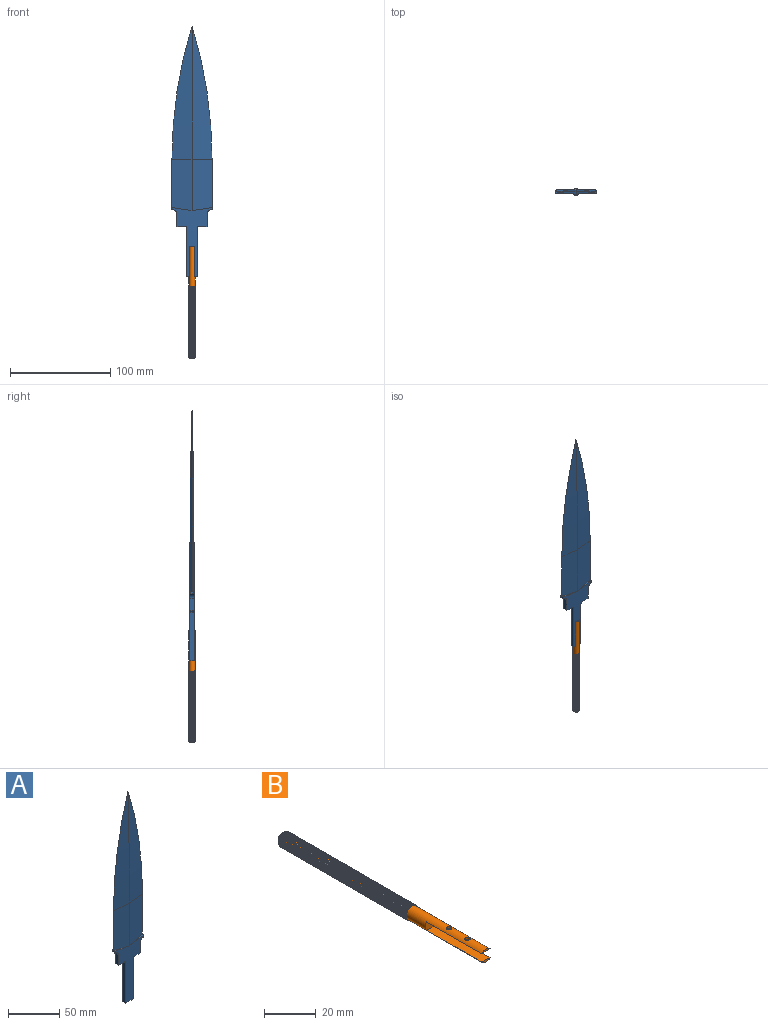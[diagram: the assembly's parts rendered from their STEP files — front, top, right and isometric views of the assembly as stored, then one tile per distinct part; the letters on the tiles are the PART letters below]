
ASSEMBLY  parts=2 mates=1
PART A: 31 faces, bbox 40.1x4.1x250.1 mm
  f0: plane 51x20mm, normal (0.1,-1,0), area 994.9mm2, adj f1,f2,f3,f21
  f1: plane 51x20mm, normal (-0.1,-1,0), area 994.9mm2, adj f0,f4,f5,f8
  f2: plane 51x20mm, normal (0.1,1,0), area 994.9mm2, adj f0,f5,f6,f10
  f3: cone r=432.23mm half-angle=84.3deg, axis (0,1,0), area 1790.2mm2, adj f0,f4,f6
  f4: cone r=452.22mm half-angle=84.3deg, axis (0,1,0), area 1790.2mm2, adj f1,f3,f7
  f5: plane 51x20mm, normal (-0.1,1,0), area 994.9mm2, adj f1,f2,f7,f9
  f6: cone r=452.22mm half-angle=84.3deg, axis (0,-1,0), area 1790.2mm2, adj f2,f3,f7
  f7: cone r=432.23mm half-angle=84.3deg, axis (0,-1,0), area 1790.2mm2, adj f4,f5,f6
  f8: plane 20.06x3.06mm, normal (0.15,0,0.99), area 20mm2, adj f1,f22,f25,f30
  f9: plane 20.06x3.06mm, normal (0.15,0,0.99), area 20mm2, adj f5,f22,f26,f28
  f10: plane 20.06x3.06mm, normal (-0.15,0,0.99), area 20mm2, adj f2,f20,f26,f27
  f11: plane 7.88x4mm, normal (0,0,-1), area 31.5mm2, adj f12,f24,f25,f26
  f12: cylinder r=2.12mm len=4mm, axis (0,1,0), area 13.3mm2, adj f11,f13,f25,f26
  f13: plane 47.88x4mm, normal (-1,0,0), area 191.5mm2, adj f12,f14,f25,f26
  f14: plane 10x4mm, normal (0,0,-1), area 40mm2, adj f13,f15,f25,f26
  f15: plane 47.88x4mm, normal (1,0,0), area 191.5mm2, adj f14,f16,f25,f26
  f16: cylinder r=2.12mm len=4mm, axis (0,1,0), area 13.3mm2, adj f15,f17,f25,f26
  f17: plane 7.88x4mm, normal (0,0,-1), area 31.5mm2, adj f16,f18,f25,f26
  f18: plane 12x4mm, normal (1,0,0), area 48mm2, adj f17,f19,f25,f26
  f19: cylinder r=5mm len=5mm, axis (0,1,0), area 31mm2, adj f18,f20,f25,f26,f27,f29
  f20: plane 2x2mm, normal (1,0,0), area 4mm2, adj f10,f19,f21,f27,f29
  f21: plane 20.06x3.06mm, normal (-0.15,0,0.99), area 20mm2, adj f0,f20,f25,f29
  f22: plane 2x2mm, normal (-1,0,0), area 4mm2, adj f8,f9,f23,f28,f30
  f23: cylinder r=5mm len=5mm, axis (0,1,0), area 31mm2, adj f22,f24,f25,f26,f28,f30
  f24: plane 12x4mm, normal (-1,0,0), area 48mm2, adj f11,f23,f25,f26
  f25: plane 68.85x38mm, normal (0,-1,0), area 1038.7mm2, adj f8,f11,f12,f13,f14,f15,f16,f17
  f26: plane 68.85x38mm, normal (0,1,0), area 1038.7mm2, adj f9,f10,f11,f12,f13,f14,f15,f16
  f27: cylinder r=1mm len=2.1mm, axis (0,0,1), area 3.1mm2, adj f10,f19,f20,f26
  f28: cylinder r=1mm len=2.1mm, axis (0,0,-1), area 3.1mm2, adj f9,f22,f23,f26
  f29: cylinder r=1mm len=2.1mm, axis (0,0,-1), area 3.1mm2, adj f19,f20,f21,f25
  f30: cylinder r=1mm len=2.1mm, axis (0,0,1), area 3.1mm2, adj f8,f22,f23,f25
PART B: 84 faces, bbox 6.6x111x7.6 mm
  f0: cylinder r=3mm len=6mm, axis (0,1,0), area 12.6mm2, adj f69,f77,f79,f81,f83
  f1: cylinder r=3mm len=41.68mm, axis (0,1,0), area 500.5mm2, adj f2,f70,f71,f72,f73,f74,f75,f76
  f2: cylinder r=3mm len=6mm, axis (0,1,0), area 11.3mm2, adj f1,f3,f79,f81
  f3: cylinder r=3mm len=6mm, axis (0,1,0), area 11.3mm2, adj f2,f4,f79,f81
  f4: cylinder r=3mm len=6mm, axis (0,1,0), area 11.3mm2, adj f3,f5,f79,f81
  f5: cylinder r=3mm len=6mm, axis (0,1,0), area 11.3mm2, adj f4,f6,f79,f81
  f6: cylinder r=3mm len=6mm, axis (0,1,0), area 11.3mm2, adj f5,f7,f79,f81
  f7: cylinder r=3mm len=6mm, axis (0,1,0), area 11.3mm2, adj f6,f8,f79,f81
  f8: cylinder r=3mm len=6mm, axis (0,1,0), area 11.3mm2, adj f7,f9,f79,f81
  f9: cylinder r=3mm len=6mm, axis (0,1,0), area 11.3mm2, adj f8,f10,f79,f81
  f10: cylinder r=3mm len=6mm, axis (0,1,0), area 11.3mm2, adj f9,f11,f79,f81
  f11: cylinder r=3mm len=6mm, axis (0,1,0), area 11.3mm2, adj f10,f12,f79,f81
  f12: cylinder r=3mm len=6mm, axis (0,1,0), area 11.3mm2, adj f11,f13,f79,f81
  f13: cylinder r=3mm len=6mm, axis (0,1,0), area 11.3mm2, adj f12,f14,f79,f81
  f14: cylinder r=3mm len=6mm, axis (0,1,0), area 11.3mm2, adj f13,f15,f79,f81
  f15: cylinder r=3mm len=6mm, axis (0,1,0), area 11.3mm2, adj f14,f16,f79,f81
  f16: cylinder r=3mm len=6mm, axis (0,1,0), area 11.3mm2, adj f15,f17,f79,f81
  f17: cylinder r=3mm len=6mm, axis (0,1,0), area 11.3mm2, adj f16,f18,f79,f81
  f18: cylinder r=3mm len=6mm, axis (0,1,0), area 11.3mm2, adj f17,f19,f79,f81
  f19: cylinder r=3mm len=6mm, axis (0,1,0), area 11.3mm2, adj f18,f20,f79,f81
  f20: cylinder r=3mm len=6mm, axis (0,1,0), area 11.3mm2, adj f19,f21,f79,f81
  f21: cylinder r=3mm len=6mm, axis (0,1,0), area 11.3mm2, adj f20,f22,f79,f81
  f22: cylinder r=3mm len=6mm, axis (0,1,0), area 11.3mm2, adj f21,f23,f79,f81
  f23: cylinder r=3mm len=6mm, axis (0,1,0), area 11.3mm2, adj f22,f24,f79,f81
  f24: cylinder r=3mm len=6mm, axis (0,1,0), area 11.3mm2, adj f23,f25,f79,f81
  f25: cylinder r=3mm len=6mm, axis (0,1,0), area 11.3mm2, adj f24,f26,f79,f81
  f26: cylinder r=3mm len=6mm, axis (0,1,0), area 11.3mm2, adj f25,f27,f79,f81
  f27: cylinder r=3mm len=6mm, axis (0,1,0), area 11.3mm2, adj f26,f28,f79,f81
  f28: cylinder r=3mm len=6mm, axis (0,1,0), area 11.3mm2, adj f27,f29,f79,f81
  f29: cylinder r=3mm len=6mm, axis (0,1,0), area 11.3mm2, adj f28,f30,f79,f81
  f30: cylinder r=3mm len=6mm, axis (0,1,0), area 11.3mm2, adj f29,f31,f79,f81
  f31: cylinder r=3mm len=6mm, axis (0,1,0), area 11.3mm2, adj f30,f32,f79,f81
  f32: cylinder r=3mm len=6mm, axis (0,1,0), area 11.3mm2, adj f31,f33,f79,f81
  f33: cylinder r=3mm len=6mm, axis (0,1,0), area 11.3mm2, adj f32,f34,f79,f81
  f34: cylinder r=3mm len=6mm, axis (0,1,0), area 11.3mm2, adj f33,f35,f79,f81
  f35: cylinder r=3mm len=6mm, axis (0,1,0), area 11.3mm2, adj f34,f36,f79,f81
  f36: cylinder r=3mm len=6mm, axis (0,1,0), area 11.3mm2, adj f35,f37,f79,f81
  f37: cylinder r=3mm len=6mm, axis (0,1,0), area 11.3mm2, adj f36,f38,f79,f81
  f38: cylinder r=3mm len=6mm, axis (0,1,0), area 11.3mm2, adj f37,f39,f79,f81
  f39: cylinder r=3mm len=6mm, axis (0,1,0), area 11.3mm2, adj f38,f40,f79,f81
  f40: cylinder r=3mm len=6mm, axis (0,1,0), area 11.3mm2, adj f39,f41,f79,f81
  f41: cylinder r=3mm len=6mm, axis (0,1,0), area 11.3mm2, adj f40,f42,f79,f81
  f42: cylinder r=3mm len=6mm, axis (0,1,0), area 11.3mm2, adj f41,f43,f79,f81
  f43: cylinder r=3mm len=6mm, axis (0,1,0), area 11.3mm2, adj f42,f44,f79,f81
  f44: cylinder r=3mm len=6mm, axis (0,1,0), area 11.3mm2, adj f43,f45,f79,f81
  f45: cylinder r=3mm len=6mm, axis (0,1,0), area 11.3mm2, adj f44,f46,f79,f81
  f46: cylinder r=3mm len=6mm, axis (0,1,0), area 11.3mm2, adj f45,f47,f79,f81
  f47: cylinder r=3mm len=6mm, axis (0,1,0), area 11.3mm2, adj f46,f48,f79,f81
  f48: cylinder r=3mm len=6mm, axis (0,1,0), area 11.3mm2, adj f47,f49,f79,f81
  f49: cylinder r=3mm len=6mm, axis (0,1,0), area 11.3mm2, adj f48,f50,f79,f81
  f50: cylinder r=3mm len=6mm, axis (0,1,0), area 11.3mm2, adj f49,f51,f79,f81
  f51: cylinder r=3mm len=6mm, axis (0,1,0), area 11.3mm2, adj f50,f52,f79,f81
  f52: cylinder r=3mm len=6mm, axis (0,1,0), area 11.3mm2, adj f51,f53,f79,f81
  f53: cylinder r=3mm len=6mm, axis (0,1,0), area 11.3mm2, adj f52,f54,f79,f81
  f54: cylinder r=3mm len=6mm, axis (0,1,0), area 11.3mm2, adj f53,f55,f79,f81
  f55: cylinder r=3mm len=6mm, axis (0,1,0), area 11.3mm2, adj f54,f56,f79,f81
  f56: cylinder r=3mm len=6mm, axis (0,1,0), area 11.3mm2, adj f55,f57,f79,f81
  f57: cylinder r=3mm len=6mm, axis (0,1,0), area 11.3mm2, adj f56,f58,f79,f81
  f58: cylinder r=3mm len=6mm, axis (0,1,0), area 11.3mm2, adj f57,f59,f79,f81
  f59: cylinder r=3mm len=6mm, axis (0,1,0), area 11.3mm2, adj f58,f60,f79,f81
  f60: cylinder r=3mm len=6mm, axis (0,1,0), area 11.3mm2, adj f59,f61,f79,f81
  f61: cylinder r=3mm len=6mm, axis (0,1,0), area 11.3mm2, adj f60,f62,f79,f81
  f62: cylinder r=3mm len=6mm, axis (0,1,0), area 11.3mm2, adj f61,f63,f79,f81
  f63: cylinder r=3mm len=6mm, axis (0,1,0), area 11.3mm2, adj f62,f64,f79,f81
  f64: cylinder r=3mm len=6mm, axis (0,1,0), area 11.3mm2, adj f63,f65,f79,f81
  f65: cylinder r=3mm len=6mm, axis (0,1,0), area 11.3mm2, adj f64,f66,f79,f81
  f66: cylinder r=3mm len=6mm, axis (0,1,0), area 11.3mm2, adj f65,f67,f79,f81
  f67: cylinder r=3mm len=6mm, axis (0,1,0), area 11.3mm2, adj f66,f68,f79,f81
  f68: cylinder r=3mm len=6mm, axis (0,1,0), area 11.3mm2, adj f67,f69,f79,f81
  f69: cylinder r=3mm len=6mm, axis (0,1,0), area 11.3mm2, adj f0,f68,f79,f81
  f70: plane 30x4.47mm, normal (0,0,-1), area 127.9mm2, adj f1,f71,f72,f75,f76
  f71: plane 4.47x1mm, normal (0,-1,0), area 3.1mm2, adj f1,f70
  f72: plane 6x4mm, normal (0,-1,0), area 22.1mm2, adj f1,f70,f73
  f73: plane 30x4.47mm, normal (0,0,1), area 134.2mm2, adj f1,f72,f74
  f74: plane 4.47x1mm, normal (0,-1,0), area 3.1mm2, adj f1,f73
  f75: cylinder r=1mm len=2mm, axis (0,0,-1), area 5.7mm2, adj f1,f70
  f76: cylinder r=1mm len=2mm, axis (0,0,-1), area 5.7mm2, adj f1,f70
  f77: plane 0.4x0.3mm, normal (0,0,-1), area 0.1mm2, adj f0,f79,f80,f81
  f78: plane 0.4x0.3mm, normal (0,0,1), area 0.1mm2, adj f1,f79,f80,f81
  f79: bspline ~70.1x7.62mm, area 439.3mm2, adj f0,f1,f2,f3,f4,f5,f6,f7
  f80: cylinder r=3.3mm len=70.2mm, axis (0,-1,0), area 290.3mm2, adj f77,f78,f79,f81
  f81: bspline ~70.1x7.62mm, area 438.6mm2, adj f0,f1,f2,f3,f4,f5,f6,f7
  f82: plane 4.6x4.6mm, normal (0,1,0), area 16.6mm2, adj f83
  f83: cone r=3mm half-angle=45deg, axis (0,-1,0), area 16.5mm2, adj f0,f82
PLACE A t=(-81.18,26.14,14.19)mm
PLACE B rot(axis=(-1,0,0),90deg) t=(-61.18,24.14,-35.81)mm
MATE fastened B.f0 <-> A.f14  axis (0,0,1) through (-61.18,24.14,-35.81)mm
